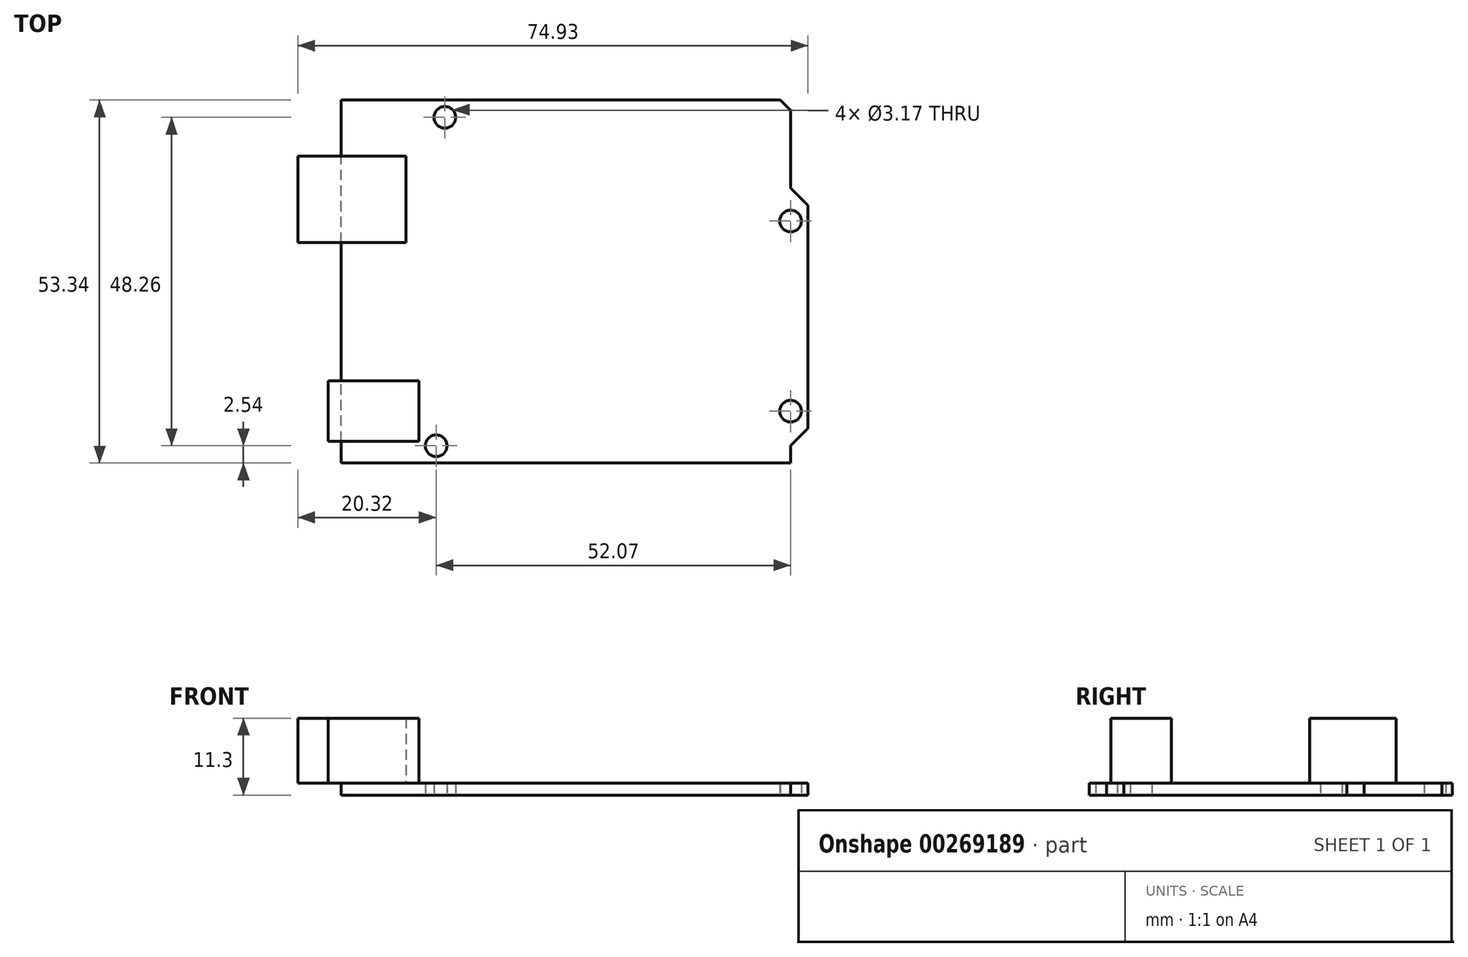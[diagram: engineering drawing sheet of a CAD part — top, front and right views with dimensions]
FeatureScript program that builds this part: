
annotation { "Feature Type Name" : "Feature", "Feature Type Description" : "" }
export const myFeature = defineFeature(function(context is Context, id is Id, definition is map)
    precondition{}
    {
        {
            var Q0;
            Q0=qCreatedBy(makeId("Top.planeOp"),FACE);
            var sketch = newSketch(context, id + "F0", { "sketchPlane" : qUnion([Q0])});
            skLineSegment(sketch, "E0", {"start": v(0, 0) * mm, "end": v(0, 53.34) * mm});
            skLineSegment(sketch, "E1", {"start": v(0, 0) * mm, "end": v(66.04, 0) * mm});
            skLineSegment(sketch, "E2", {"start": v(66.04, 0) * mm, "end": v(66.04, 2.54) * mm});
            skLineSegment(sketch, "E3", {"start": v(66.04, 2.54) * mm, "end": v(68.58, 5.08) * mm});
            skLineSegment(sketch, "E4", {"start": v(68.58, 5.08) * mm, "end": v(68.58, 37.85) * mm});
            skLineSegment(sketch, "E5", {"start": v(66.04, 40.39) * mm, "end": v(68.58, 37.85) * mm});
            skLineSegment(sketch, "E6", {"start": v(66.04, 40.39) * mm, "end": v(66.04, 51.82) * mm});
            skLineSegment(sketch, "E7", {"start": v(0, 53.34) * mm, "end": v(64.52, 53.34) * mm});
            skLineSegment(sketch, "E8", {"start": v(66.04, 51.82) * mm, "end": v(64.52, 53.34) * mm});
            skLineSegment(sketch, "E9", {"start": v(68.58, 7.62) * mm, "end": v(66.04, 7.62) * mm});
            skCircle(sketch, "E10", {"center": v(66.04, 7.62) * mm, "radius": 1.59 * mm});
            skCircle(sketch, "E11", {"center": v(13.97, 2.54) * mm, "radius": 1.59 * mm});
            skLineSegment(sketch, "E12", {"start": v(13.65, 50.8) * mm, "end": v(15.24, 50.8) * mm});
            skCircle(sketch, "E13", {"center": v(15.24, 50.8) * mm, "radius": 1.59 * mm});
            skLineSegment(sketch, "E14", {"start": v(66.04, 0) * mm, "end": v(66.04, 35.56) * mm});
            skCircle(sketch, "E15", {"center": v(66.04, 35.56) * mm, "radius": 1.59 * mm});
            skSolve(sketch);
        }
        {
            var Q0;
            Q0=qSketchRegion(id+"F0",true);
            extrude(context, id + "F1", {"entities" : qUnion([Q0]), "depth" : 1.78 * mm});
        }
        {
            var Q0;
            Q0=makeQuery(id+"F1.opExtrude","CAP_FACE",FACE,{"disambiguationData":[OSD([sQuery(id+"F0.wireOp",EDGE,"E0"),sQuery(id+"F0.wireOp",EDGE,"E1"),sQuery(id+"F0.wireOp",EDGE,"E3"),sQuery(id+"F0.wireOp",EDGE,"E4"),sQuery(id+"F0.wireOp",EDGE,"E5"),sQuery(id+"F0.wireOp",EDGE,"E6"),sQuery(id+"F0.wireOp",EDGE,"E7"),sQuery(id+"F0.wireOp",EDGE,"E8"),sQuery(id+"F0.wireOp",EDGE,"E10"),sQuery(id+"F0.wireOp",EDGE,"E11"),sQuery(id+"F0.wireOp",EDGE,"E13"),sQuery(id+"F0.wireOp",EDGE,"E14"),sQuery(id+"F0.wireOp",EDGE,"E15")])],"isStart":false});
            var sketch = newSketch(context, id + "F2", { "sketchPlane" : qUnion([Q0])});
            skLineSegment(sketch, "E16", {"start": v(9.53, 32.39) * mm, "end": v(0, 32.39) * mm});
            skLineSegment(sketch, "E17", {"start": v(9.53, 32.39) * mm, "end": v(9.53, 45.09) * mm});
            skLineSegment(sketch, "E18", {"start": v(9.53, 45.09) * mm, "end": v(-6.35, 45.09) * mm});
            skLineSegment(sketch, "E19", {"start": v(0, 32.39) * mm, "end": v(-6.35, 32.39) * mm});
            skLineSegment(sketch, "E20", {"start": v(-6.35, 32.39) * mm, "end": v(-6.35, 45.09) * mm});
            skLineSegment(sketch, "E21", {"start": v(11.43, 3.18) * mm, "end": v(0, 3.17) * mm});
            skLineSegment(sketch, "E22", {"start": v(11.43, 3.17) * mm, "end": v(11.43, 12.06) * mm});
            skLineSegment(sketch, "E23", {"start": v(11.43, 12.06) * mm, "end": v(-1.9, 12.06) * mm});
            skLineSegment(sketch, "E24", {"start": v(0, 3.18) * mm, "end": v(-1.9, 3.18) * mm});
            skLineSegment(sketch, "E25", {"start": v(-1.9, 3.18) * mm, "end": v(-1.9, 12.06) * mm});
            skSolve(sketch);
        }
        {
            var Q0;
            Q0=qSketchRegion(id+"F2",true);
            extrude(context, id + "F3", {"entities" : qUnion([Q0]), "operationType" : NewBodyOperationType.ADD, "depth" : 9.52 * mm});
        }
    });
